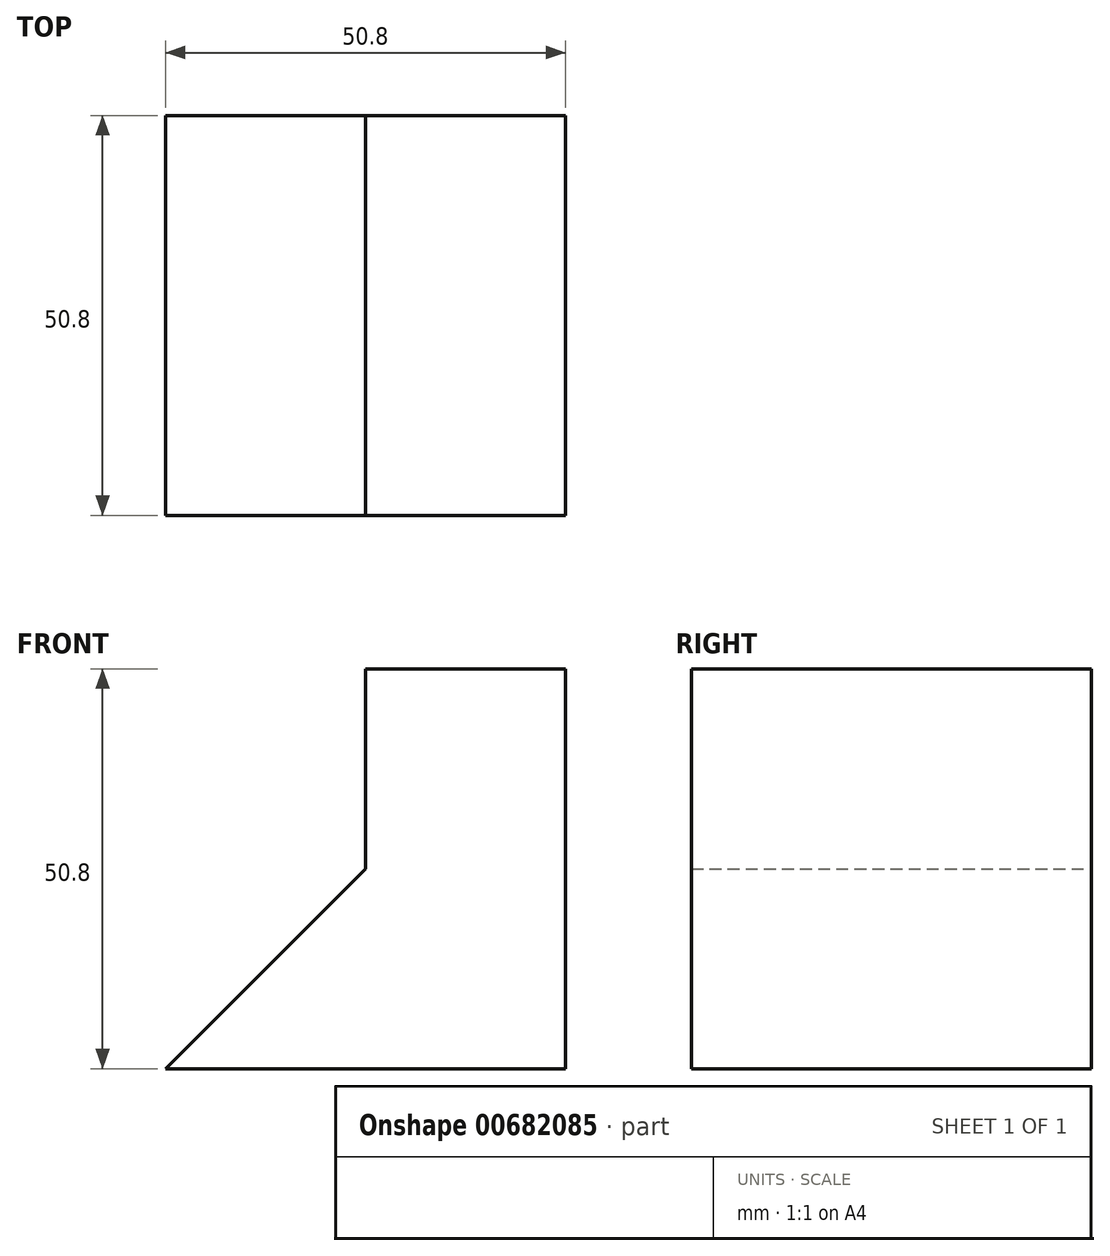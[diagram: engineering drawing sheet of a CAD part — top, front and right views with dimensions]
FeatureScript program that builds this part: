
annotation { "Feature Type Name" : "Feature", "Feature Type Description" : "" }
export const myFeature = defineFeature(function(context is Context, id is Id, definition is map)
    precondition{}
    {
        {
            var Q0;
            Q0=qCreatedBy(makeId("Front.planeOp"),FACE);
            var sketch = newSketch(context, id + "F0", { "sketchPlane" : qUnion([Q0])});
            skLineSegment(sketch, "E0", {"start": v(0, 0) * mm, "end": v(50.8, 0) * mm});
            skLineSegment(sketch, "E1", {"start": v(50.8, 0) * mm, "end": v(50.8, 50.8) * mm});
            skLineSegment(sketch, "E2", {"start": v(50.8, 50.8) * mm, "end": v(25.4, 50.8) * mm});
            skLineSegment(sketch, "E3", {"start": v(25.4, 50.8) * mm, "end": v(25.4, 25.4) * mm});
            skLineSegment(sketch, "E4", {"start": v(25.4, 25.4) * mm, "end": v(0, 0) * mm});
            skSolve(sketch);
        }
        {
            var Q0;
            Q0 = qSketchRegion(id + "F0", true);
            extrude(context, id + "F1", {"entities" : qUnion([Q0]), "depth" : 50.8 * mm, "offsetDistance" : 25.4 * mm});
        }
    });
